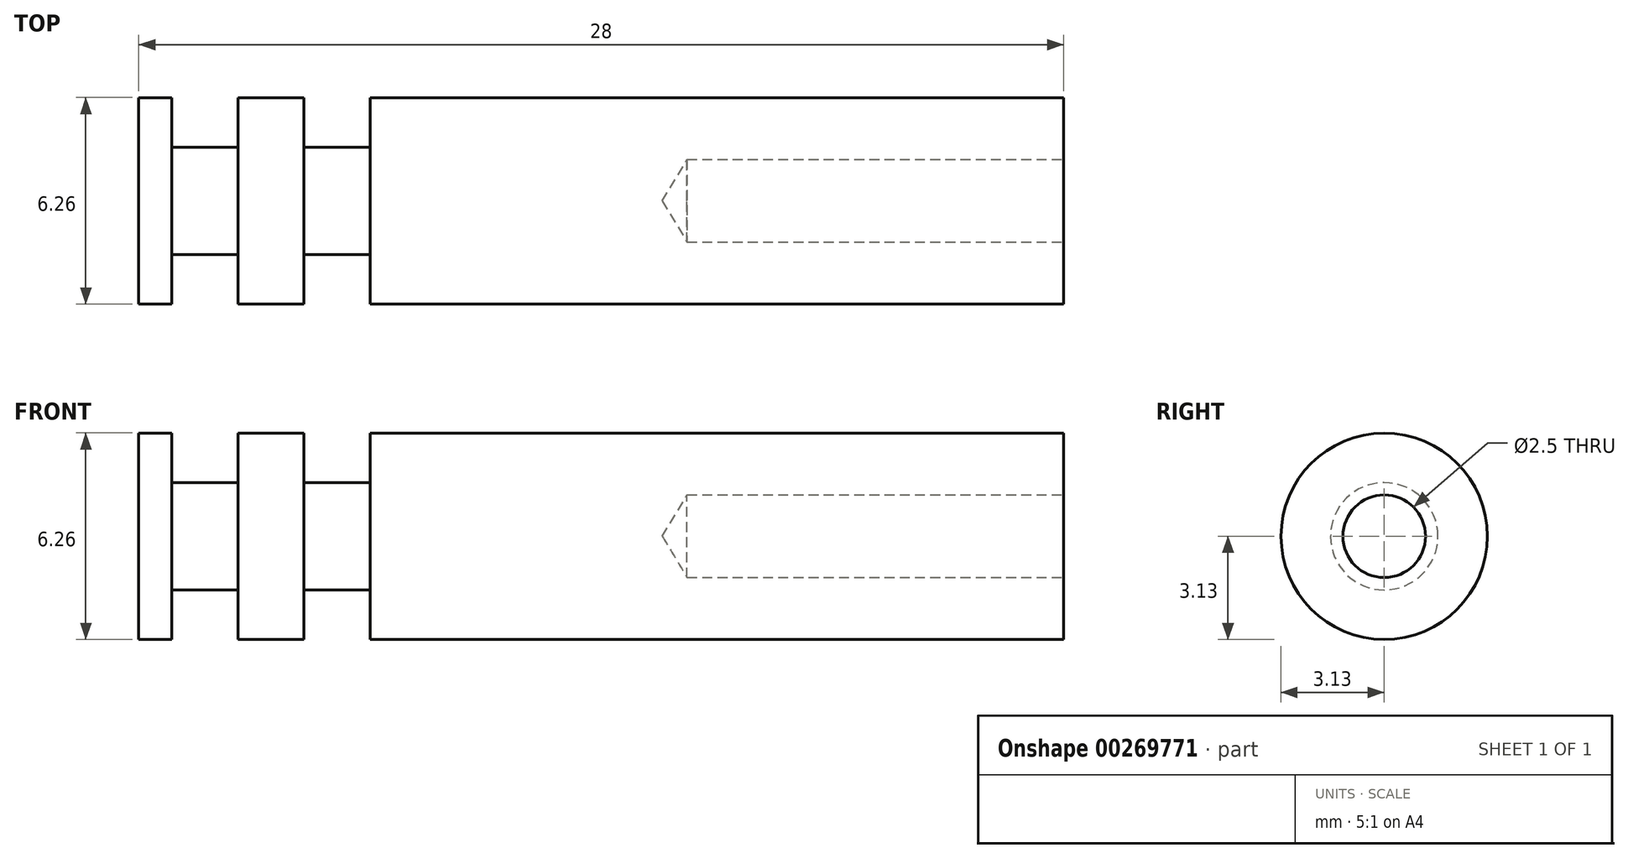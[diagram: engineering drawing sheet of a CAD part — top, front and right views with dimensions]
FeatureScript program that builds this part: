
annotation { "Feature Type Name" : "Feature", "Feature Type Description" : "" }
export const myFeature = defineFeature(function(context is Context, id is Id, definition is map)
    precondition{}
    {
        {
            var Q0;
            Q0=qCreatedBy(makeId("Right.planeOp"),FACE);
            var sketch = newSketch(context, id + "F0", { "sketchPlane" : qUnion([Q0])});
            skCircle(sketch, "E0", {"center": v(0, 0) * mm, "radius": 3.12 * mm});
            skSolve(sketch);
        }
        {
            var Q0;
            Q0=makeQuery(id+"F0.imprint","IMPRINT",FACE,{"disambiguationData":[TD([[makeQuery(id+"F0.imprint","IMPRINT",EDGE,{"derivedFrom":sQuery(id+"F0.wireOp",EDGE,"E0")}),1.0]])]});
            extrude(context, id + "F1", {"entities" : qUnion([Q0]), "depth" : 28 * mm});
        }
        {
            var Q0;
            Q0=qCreatedBy(makeId("Front.planeOp"),FACE);
            var sketch = newSketch(context, id + "F2", { "sketchPlane" : qUnion([Q0])});
            skLineSegment(sketch, "E1.bottom", {"start": v(3, 1.63) * mm, "end": v(1, 1.63) * mm});
            skLineSegment(sketch, "E1.top", {"start": v(3, 6.77) * mm, "end": v(1, 6.77) * mm});
            skLineSegment(sketch, "E1.left", {"start": v(3, 1.63) * mm, "end": v(3, 6.77) * mm});
            skLineSegment(sketch, "E1.right", {"start": v(1, 1.63) * mm, "end": v(1, 6.77) * mm});
            skPoint(sketch, "E1.middle", {"position": v(2, 4.2) * mm});
            skPoint(sketch, "E2.1.0.0", {"position": v(6, 4.2) * mm});
            skLineSegment(sketch, "E2.1.0.1", {"start": v(7, 1.63) * mm, "end": v(7, 6.77) * mm});
            skLineSegment(sketch, "E2.1.0.2", {"start": v(5, 1.63) * mm, "end": v(5, 6.77) * mm});
            skLineSegment(sketch, "E2.1.0.3", {"start": v(7, 6.77) * mm, "end": v(5, 6.77) * mm});
            skLineSegment(sketch, "E2.1.0.4", {"start": v(7, 1.63) * mm, "end": v(5, 1.63) * mm});
            skLineSegment(sketch, "E2.direction1", {"start": v(1, 1.63) * mm, "end": v(5, 1.63) * mm, "construction": true});
            skSolve(sketch);
        }
        {
            var Q0;
            Q0 = qSketchRegion(id + "F2", true);
            var Q1;
            Q1=makeQuery(id+"F1.opExtrude","SWEPT_FACE",FACE,{"disambiguationData":[OSD([sQuery(id+"F0.wireOp",EDGE,"E0")])]});
            revolve(context, id + "F3", {"operationType" : NewBodyOperationType.REMOVE, "entities" : qUnion([Q0]), "axis" : qUnion([Q1]), "revolveType" : RevolveType.FULL, "oppositeDirection" : true});
        }
        {
            var Q0;
            Q0=makeQuery(id+"F1.opExtrude","CAP_FACE",FACE,{"disambiguationData":[OSD([sQuery(id+"F0.wireOp",EDGE,"E0")])],"isStart":false});
            var sketch = newSketch(context, id + "F4", { "sketchPlane" : qUnion([Q0])});
            skPoint(sketch, "E3", {"position": v(0, 0) * mm});
            skSolve(sketch);
        }
        {
            var Q0;
            Q0=sQuery(id+"F4.wireOp",VERTEX,"E3");
            var Q1;
            Q1=makeQuery(id+"F1.opExtrude","SWEPT_BODY",BODY,{"disambiguationData":[OSD([sQuery(id+"F0.wireOp",EDGE,"E0")])]});
            hole(context, id + "F5", {"style" : HoleStyle.SIMPLE, "endStyle" : HoleEndStyle.BLIND, "standardTappedOrClearance" : lookupTablePath({ "standard" : "ISO", "engagement" : "75%", "pitch" : "0.5 mm", "size" : "M3", "type" : "Tapped" }), "standardBlindInLast" : lookupTablePath({ "standard" : "ISO", "engagement" : "75%", "pitch" : "0.5 mm", "size" : "M3", "type" : "Tapped" }), "holeDiameter" : 2.5 * mm, "showTappedDepth" : true, "holeDepth" : 11.4 * mm, "tappedDepth" : 9.9 * mm, "tapClearance" : 3, "locations" : qUnion([Q0]), "scope" : qUnion([Q1]), "majorDiameter" : 3 * mm});
        }
    });
